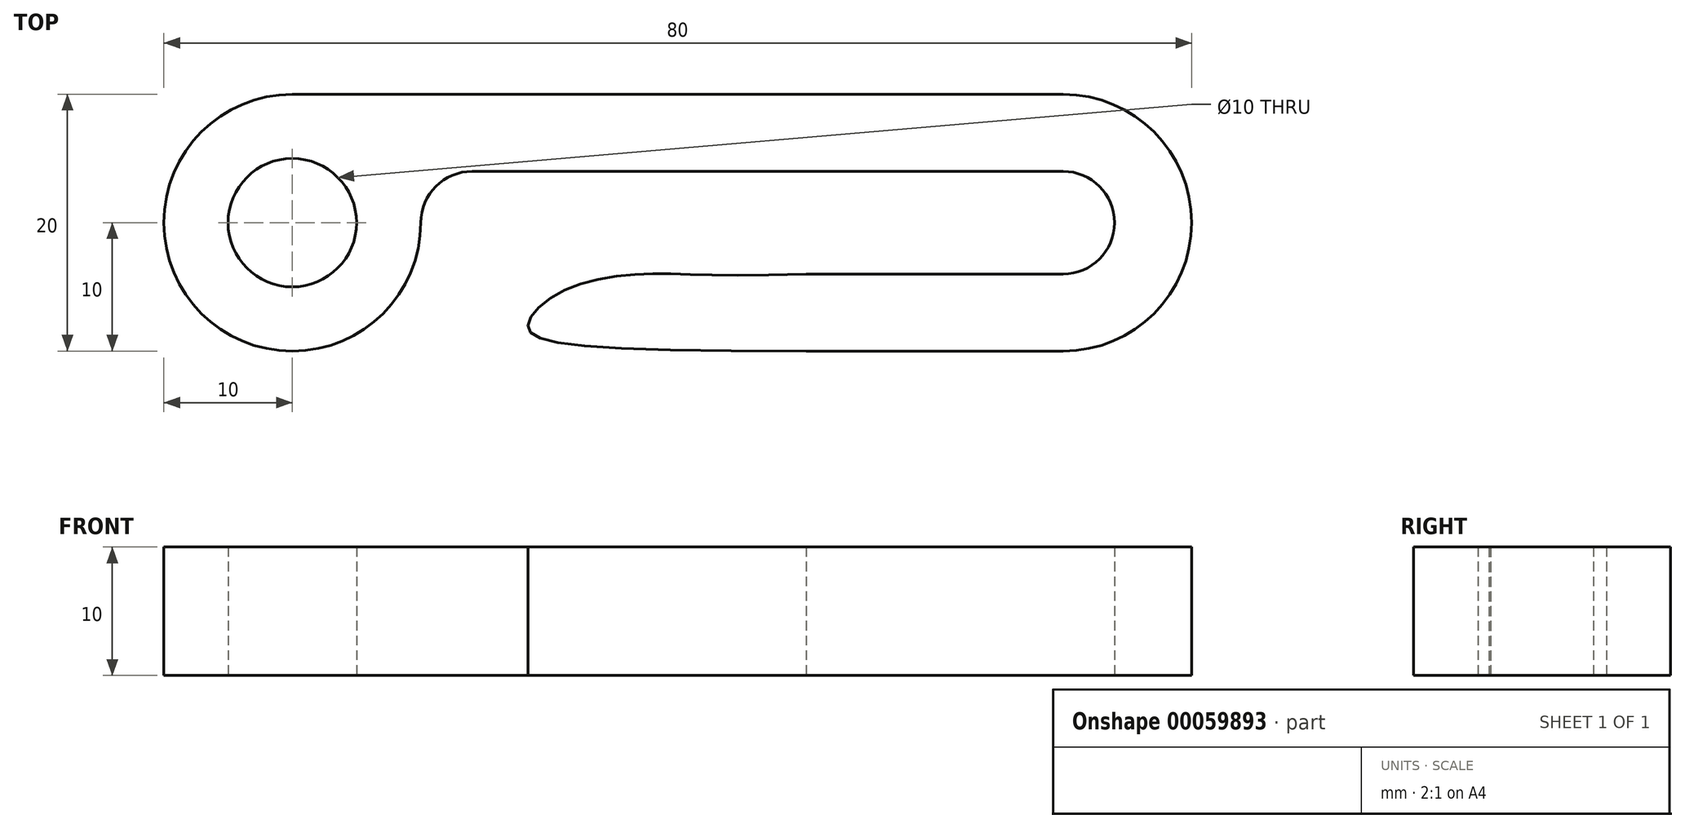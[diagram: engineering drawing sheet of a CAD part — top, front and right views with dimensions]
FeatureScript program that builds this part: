
annotation { "Feature Type Name" : "Feature", "Feature Type Description" : "" }
export const myFeature = defineFeature(function(context is Context, id is Id, definition is map)
    precondition{}
    {
        {
            var Q0;
            Q0=qCreatedBy(makeId("Top.planeOp"),FACE);
            var sketch = newSketch(context, id + "F0", { "sketchPlane" : qUnion([Q0])});
            skCircle(sketch, "E0", {"center": v(-40, 10) * mm, "radius": 5 * mm});
            skCircle(sketch, "E1", {"center": v(-40, 10) * mm, "radius": 10 * mm});
            skLineSegment(sketch, "E2", {"start": v(-40, 20) * mm, "end": v(20, 20) * mm});
            skArc(sketch, "E3", {"start": v(20, 20) * mm, "mid": v(30, 10) * mm, "end": v(20, 0) * mm});
            skLineSegment(sketch, "E4", {"start": v(0, 0) * mm, "end": v(20, 0) * mm});
            skArc(sketch, "E5", {"start": v(20, 14) * mm, "mid": v(24, 10) * mm, "end": v(20, 6) * mm});
            skLineSegment(sketch, "E6", {"start": v(20, 14) * mm, "end": v(-26, 14) * mm});
            skLineSegment(sketch, "E7", {"start": v(20, 6) * mm, "end": v(0, 6) * mm});
            skFitSpline(sketch, "E8", {"points": [v(0, 0) * mm, v(-21.6, 2.3) * mm, v(-18.88, 4.71) * mm, v(-12.55, 6) * mm, v(0, 6) * mm], "startDerivative": vector(-147, 0) * mm, "endDerivative": vector(73.67, 2.71) * mm});
            skArc(sketch, "E9", {"start": v(-26, 14) * mm, "mid": v(-28.83, 12.83) * mm, "end": v(-30, 10) * mm});
            skSolve(sketch);
        }
        {
            var Q0;
            Q0 = qSketchRegion(id + "F0", true);
            extrude(context, id + "F1", {"entities" : qUnion([Q0]), "depth" : 10 * mm});
        }
    });
